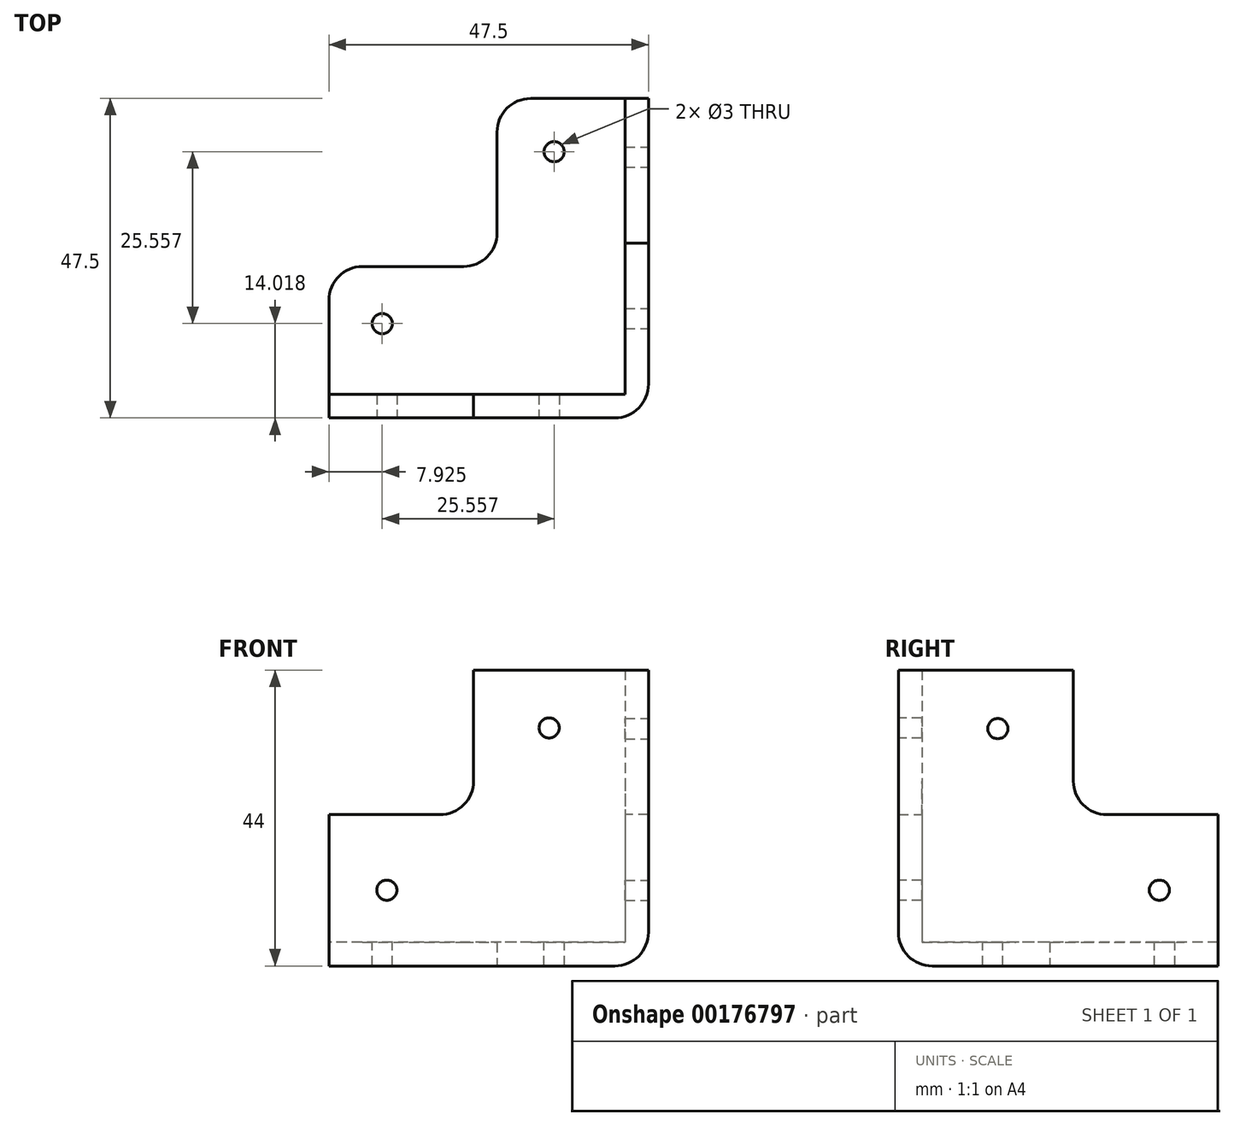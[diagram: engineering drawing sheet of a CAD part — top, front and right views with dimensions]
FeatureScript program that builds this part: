
annotation { "Feature Type Name" : "Feature", "Feature Type Description" : "" }
export const myFeature = defineFeature(function(context is Context, id is Id, definition is map)
    precondition{}
    {
        {
            var Q0;
            Q0=qCreatedBy(makeId("Top.planeOp"),FACE);
            var sketch = newSketch(context, id + "F0", { "sketchPlane" : qUnion([Q0])});
            skLineSegment(sketch, "E0", {"start": v(0, 0) * mm, "end": v(0, 25) * mm});
            skLineSegment(sketch, "E1", {"start": v(0, 25) * mm, "end": v(22.5, 25) * mm});
            skLineSegment(sketch, "E2", {"start": v(22.5, 25) * mm, "end": v(22.5, 0) * mm});
            skLineSegment(sketch, "E3", {"start": v(22.5, 0) * mm, "end": v(22.5, -22.5) * mm});
            skLineSegment(sketch, "E4", {"start": v(22.5, -22.5) * mm, "end": v(0, -22.5) * mm});
            skLineSegment(sketch, "E5", {"start": v(0, -22.5) * mm, "end": v(-25, -22.5) * mm});
            skLineSegment(sketch, "E6", {"start": v(-25, -22.5) * mm, "end": v(-25, 0) * mm});
            skLineSegment(sketch, "E7", {"start": v(-25, 0) * mm, "end": v(0, 0) * mm});
            skSolve(sketch);
        }
        {
            var Q0;
            Q0=makeQuery(id+"F0.imprint","IMPRINT",FACE,{"disambiguationData":[TD([[makeQuery(id+"F0.imprint","IMPRINT",EDGE,{"derivedFrom":sQuery(id+"F0.wireOp",EDGE,"E0")}),-1.0]])]});
            extrude(context, id + "F1", {"entities" : qUnion([Q0]), "depth" : 44 * mm});
        }
        {
            var Q0;
            Q0=makeQuery(id+"F1.opExtrude","CAP_FACE",FACE,{"disambiguationData":[OSD([sQuery(id+"F0.wireOp",EDGE,"E0"),sQuery(id+"F0.wireOp",EDGE,"E1"),sQuery(id+"F0.wireOp",EDGE,"E2"),sQuery(id+"F0.wireOp",EDGE,"E3"),sQuery(id+"F0.wireOp",EDGE,"E4"),sQuery(id+"F0.wireOp",EDGE,"E5"),sQuery(id+"F0.wireOp",EDGE,"E6"),sQuery(id+"F0.wireOp",EDGE,"E7")])],"isStart":false});
            var Q1;
            Q1=makeQuery(id+"F1.opExtrude","SWEPT_FACE",FACE,{"disambiguationData":[OSD([sQuery(id+"F0.wireOp",EDGE,"E0")])]});
            var Q2;
            Q2=makeQuery(id+"F1.opExtrude","SWEPT_FACE",FACE,{"disambiguationData":[OSD([sQuery(id+"F0.wireOp",EDGE,"E7")])]});
            var Q3;
            Q3=makeQuery(id+"F1.opExtrude","SWEPT_FACE",FACE,{"disambiguationData":[OSD([sQuery(id+"F0.wireOp",EDGE,"E6")])]});
            var Q4;
            Q4=makeQuery(id+"F1.opExtrude","SWEPT_FACE",FACE,{"disambiguationData":[OSD([sQuery(id+"F0.wireOp",EDGE,"E1")])]});
            shell(context, id + "F2", {"entities" : qUnion([Q0, Q1, Q2, Q3, Q4]), "thickness" : 3.5 * mm});
        }
        {
            var Q0;
            Q0=makeQuery(id+"F2.opShell","OFFSET_FACE",FACE,{"disambiguationData":[OSD([sQuery(id+"F0.wireOp",EDGE,"E2"),sQuery(id+"F0.wireOp",EDGE,"E3")])]});
            var sketch = newSketch(context, id + "F3", { "sketchPlane" : qUnion([Q0])});
            skLineSegment(sketch, "E8.bottom", {"start": v(-25, 44) * mm, "end": v(-3.5, 44) * mm});
            skLineSegment(sketch, "E8.left", {"start": v(-25, 44) * mm, "end": v(-25, 22.5) * mm});
            skLineSegment(sketch, "E9", {"start": v(-25, 22.5) * mm, "end": v(0, 22.5) * mm});
            skPoint(sketch, "E8.top.end.orphan", {"position": v(0, 3.5) * mm});
            skLineSegment(sketch, "E10", {"start": v(-3.5, 44) * mm, "end": v(-3.5, 22.5) * mm});
            skSolve(sketch);
        }
        {
            var Q0;
            Q0=makeQuery(id+"F3.imprint","IMPRINT",FACE,{"disambiguationData":[TD([[makeQuery(id+"F3.imprint","IMPRINT",EDGE,{"derivedFrom":sQuery(id+"F3.wireOp",EDGE,"E8.bottom")}),-1.0]])]});
            var Q1;
            {var subQ0=sQuery(id+"F3.wireOp",EDGE,"E8.left");Q1=makeQuery(id+"F3.imprint","IMPRINT",FACE,{"disambiguationData":[TD([[makeQuery(id+"F3.imprint","IMPRINT",EDGE,{"derivedFrom":subQ0}),1.0]])]});}
            extrude(context, id + "F4", {"entities" : qUnion([Q0, Q1]), "operationType" : NewBodyOperationType.REMOVE, "oppositeDirection" : true, "depth" : 25 * mm});
        }
        {
            var Q0;
            Q0=makeQuery(id+"F2.opShell","OFFSET_FACE",FACE,{"disambiguationData":[OSD([sQuery(id+"F0.wireOp",EDGE,"E4"),sQuery(id+"F0.wireOp",EDGE,"E5")])]});
            var sketch = newSketch(context, id + "F5", { "sketchPlane" : qUnion([Q0])});
            skLineSegment(sketch, "E11.bottom", {"start": v(25, 44) * mm, "end": v(3.5, 44) * mm});
            skLineSegment(sketch, "E12", {"start": v(3.5, 44) * mm, "end": v(3.5, 22.5) * mm});
            skLineSegment(sketch, "E13", {"start": v(3.5, 22.5) * mm, "end": v(25, 22.5) * mm});
            skLineSegment(sketch, "E14", {"start": v(25, 22.5) * mm, "end": v(25, 44) * mm});
            skSolve(sketch);
        }
        {
            var Q0;
            Q0=makeQuery(id+"F5.imprint","IMPRINT",FACE,{"disambiguationData":[TD([[makeQuery(id+"F5.imprint","IMPRINT",EDGE,{"derivedFrom":sQuery(id+"F5.wireOp",EDGE,"E11.bottom")}),-1.0]])]});
            extrude(context, id + "F6", {"entities" : qUnion([Q0]), "operationType" : NewBodyOperationType.REMOVE, "oppositeDirection" : true, "depth" : 25 * mm});
        }
        {
            var Q0;
            Q0=makeQuery(id+"F1.opExtrude","CAP_EDGE",EDGE,{"disambiguationData":[OSD([sQuery(id+"F0.wireOp",EDGE,"E2"),sQuery(id+"F0.wireOp",EDGE,"E3")])],"isStart":true});
            var Q1;
            Q1=makeQuery(id+"F1.opExtrude","CAP_EDGE",EDGE,{"disambiguationData":[OSD([sQuery(id+"F0.wireOp",EDGE,"E4"),sQuery(id+"F0.wireOp",EDGE,"E5")])],"isStart":true});
            var Q2;
            Q2=makeQuery(id+"F1.opExtrude","SWEPT_EDGE",EDGE,{"disambiguationData":[OSD([sQuery(id+"F0.wireOp",EDGE,"E3"),sQuery(id+"F0.wireOp",EDGE,"E4")])]});
            var Q3;
            Q3=makeQuery(id+"F4.boolean.opBoolean","COPY",EDGE,{"derivedFrom":makeQuery(id+"F4.opExtrude","SWEPT_EDGE",EDGE,{"disambiguationData":[OSD([sQuery(id+"F3.wireOp",EDGE,"E8.right"),sQuery(id+"F3.wireOp",EDGE,"E9")])]})});
            var Q4;
            Q4=makeQuery(id+"F1.opExtrude","SWEPT_EDGE",EDGE,{"disambiguationData":[OSD([sQuery(id+"F0.wireOp",EDGE,"E0"),sQuery(id+"F0.wireOp",EDGE,"E7")])]});
            var Q5;
            Q5=makeQuery(id+"F6.boolean.opBoolean","COPY",EDGE,{"derivedFrom":makeQuery(id+"F6.opExtrude","SWEPT_EDGE",EDGE,{"disambiguationData":[OSD([sQuery(id+"F5.wireOp",EDGE,"E12"),sQuery(id+"F5.wireOp",EDGE,"E13")])]})});
            var Q6;
            Q6=makeQuery(id+"F1.opExtrude","SWEPT_EDGE",EDGE,{"disambiguationData":[OSD([sQuery(id+"F0.wireOp",EDGE,"E0"),sQuery(id+"F0.wireOp",EDGE,"E1")])]});
            var Q7;
            Q7=makeQuery(id+"F4.boolean.opBoolean","COPY",EDGE,{"derivedFrom":makeQuery(id+"F4.opExtrude","SWEPT_EDGE",EDGE,{"disambiguationData":[OSD([sQuery(id+"F0.wireOp",EDGE,"E1"),sQuery(id+"F0.wireOp",EDGE,"E2"),sQuery(id+"F3.wireOp",EDGE,"E8.left"),sQuery(id+"F3.wireOp",EDGE,"E9")])]})});
            var Q8;
            Q8=makeQuery(id+"F4.boolean.opBoolean","COPY",EDGE,{"derivedFrom":makeQuery(id+"F4.opExtrude","SWEPT_EDGE",EDGE,{"disambiguationData":[OSD([sQuery(id+"F0.wireOp",EDGE,"E2"),sQuery(id+"F0.wireOp",EDGE,"E3"),sQuery(id+"F3.wireOp",EDGE,"E8.bottom"),sQuery(id+"F3.wireOp",EDGE,"E8.right")])]})});
            var Q9;
            Q9=makeQuery(id+"F6.boolean.opBoolean","COPY",EDGE,{"derivedFrom":makeQuery(id+"F6.opExtrude","SWEPT_EDGE",EDGE,{"disambiguationData":[OSD([sQuery(id+"F0.wireOp",EDGE,"E4"),sQuery(id+"F0.wireOp",EDGE,"E5"),sQuery(id+"F5.wireOp",EDGE,"E11.bottom"),sQuery(id+"F5.wireOp",EDGE,"E12")])]})});
            var Q10;
            Q10=makeQuery(id+"F6.boolean.opBoolean","COPY",EDGE,{"derivedFrom":makeQuery(id+"F6.opExtrude","SWEPT_EDGE",EDGE,{"disambiguationData":[OSD([sQuery(id+"F0.wireOp",EDGE,"E5"),sQuery(id+"F0.wireOp",EDGE,"E6"),sQuery(id+"F5.wireOp",EDGE,"E13"),sQuery(id+"F5.wireOp",EDGE,"E14")])]})});
            var Q11;
            Q11=makeQuery(id+"F1.opExtrude","SWEPT_EDGE",EDGE,{"disambiguationData":[OSD([sQuery(id+"F0.wireOp",EDGE,"E6"),sQuery(id+"F0.wireOp",EDGE,"E7")])]});
            fillet(context, id + "F7", {"entities" : qUnion([Q0, Q1, Q2, Q3, Q4, Q5, Q6, Q7, Q8, Q9, Q10, Q11]), "radius" : 5 * mm, "tangentPropagation" : true, "allowEdgeOverflow" : false});
        }
        {
            var Q0;
            Q0=makeQuery(id+"F2.opShell","OFFSET_FACE",FACE,{"disambiguationData":[OSD([sQuery(id+"F0.wireOp",EDGE,"E0"),sQuery(id+"F0.wireOp",EDGE,"E1"),sQuery(id+"F0.wireOp",EDGE,"E2"),sQuery(id+"F0.wireOp",EDGE,"E3"),sQuery(id+"F0.wireOp",EDGE,"E4"),sQuery(id+"F0.wireOp",EDGE,"E5"),sQuery(id+"F0.wireOp",EDGE,"E6"),sQuery(id+"F0.wireOp",EDGE,"E7")])]});
            var sketch = newSketch(context, id + "F8", { "sketchPlane" : qUnion([Q0])});
            skCircle(sketch, "E15", {"center": v(-17.07, -8.48) * mm, "radius": 1.5 * mm});
            skLineSegment(sketch, "E16", {"start": v(-1.46, 1.46) * mm, "end": v(0, 0) * mm});
            skCircle(sketch, "E17.MirrorC", {"center": v(8.48, 17.07) * mm, "radius": 1.5 * mm});
            skSolve(sketch);
        }
        {
            var Q0;
            Q0=makeQuery(id+"F1.opExtrude","SWEPT_FACE",FACE,{"disambiguationData":[OSD([sQuery(id+"F0.wireOp",EDGE,"E2"),sQuery(id+"F0.wireOp",EDGE,"E3")])]});
            var sketch = newSketch(context, id + "F9", { "sketchPlane" : qUnion([Q0])});
            skCircle(sketch, "E18", {"center": v(-7.73, 35.28) * mm, "radius": 1.5 * mm});
            skCircle(sketch, "E19.MirrorC", {"center": v(16.28, 11.27) * mm, "radius": 1.5 * mm});
            skSolve(sketch);
        }
        {
            var Q0;
            Q0=makeQuery(id+"F1.opExtrude","SWEPT_FACE",FACE,{"disambiguationData":[OSD([sQuery(id+"F0.wireOp",EDGE,"E4"),sQuery(id+"F0.wireOp",EDGE,"E5")])]});
            var sketch = newSketch(context, id + "F10", { "sketchPlane" : qUnion([Q0])});
            skPoint(sketch, "E20.startSnap0", {"position": v(-2.04, 42.54) * mm});
            skCircle(sketch, "E21", {"center": v(7.73, 35.4) * mm, "radius": 1.5 * mm});
            skCircle(sketch, "E22.MirrorC", {"center": v(-16.4, 11.27) * mm, "radius": 1.5 * mm});
            skSolve(sketch);
        }
        {
            var Q0;
            Q0 = qSketchRegion(id + "F10", true);
            extrude(context, id + "F11", {"entities" : qUnion([Q0]), "operationType" : NewBodyOperationType.REMOVE, "oppositeDirection" : true, "depth" : 25 * mm});
        }
        {
            var Q0;
            Q0 = qSketchRegion(id + "F9", true);
            extrude(context, id + "F12", {"entities" : qUnion([Q0]), "operationType" : NewBodyOperationType.REMOVE, "oppositeDirection" : true, "depth" : 25 * mm});
        }
        {
            var Q0;
            Q0 = qSketchRegion(id + "F8", true);
            extrude(context, id + "F13", {"entities" : qUnion([Q0]), "operationType" : NewBodyOperationType.REMOVE, "oppositeDirection" : true, "depth" : 25 * mm});
        }
    });
